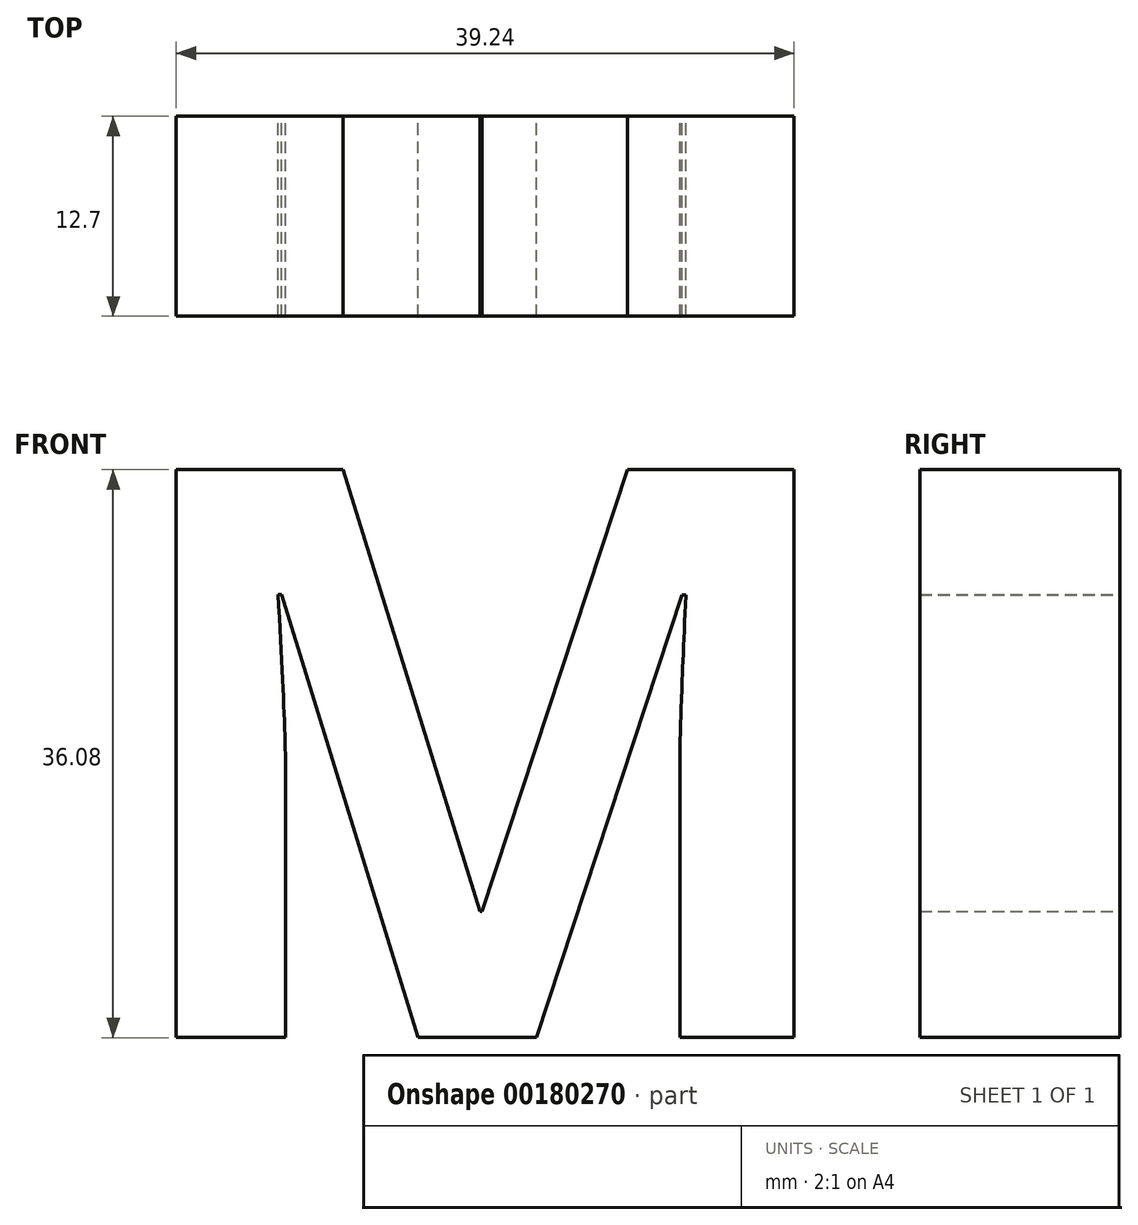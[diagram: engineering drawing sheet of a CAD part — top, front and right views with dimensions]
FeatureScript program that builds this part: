
annotation { "Feature Type Name" : "Feature", "Feature Type Description" : "" }
export const myFeature = defineFeature(function(context is Context, id is Id, definition is map)
    precondition{}
    {
        {
            var Q0;
            Q0=qCreatedBy(makeId("Front.planeOp"),FACE);
            var sketch = newSketch(context, id + "F0", { "sketchPlane" : qUnion([Q0])});
            skLineSegment(sketch, "E0.bottom", {"start": v(24, -18.34) * mm, "end": v(-24, -18.34) * mm});
            skLineSegment(sketch, "E0.top", {"start": v(24, 18.34) * mm, "end": v(-24, 18.34) * mm});
            skLineSegment(sketch, "E0.left", {"start": v(24, -18.34) * mm, "end": v(24, 18.34) * mm});
            skLineSegment(sketch, "E0.right", {"start": v(-24, -18.34) * mm, "end": v(-24, 18.34) * mm});
            skPoint(sketch, "E0.middle", {"position": v(0, 0) * mm});
            skText(sketch, "E1", { "text": "M", "fontName": "OpenSans-Bold.ttf"});
            const initialGuessF0  = {"E1": [-0.02374, -0.01897, 1, 0, 0.03702]};
            skSetInitialGuess(sketch, initialGuessF0);
            skSolve(sketch);
        }
        {
            var Q0;
            {var subQ7=sQuery(id+"F0.wireOp",EDGE,"E1.sketch_text.stroke-1");Q0=makeQuery(id+"F0.imprint","IMPRINT",FACE,{"disambiguationData":[TD([[makeQuery(id+"F0.imprint","IMPRINT",EDGE,{"derivedFrom":subQ7}),-1.0]])]});}
            extrude(context, id + "F1", {"entities" : qUnion([Q0]), "depth" : 12.7 * mm});
        }
    });
